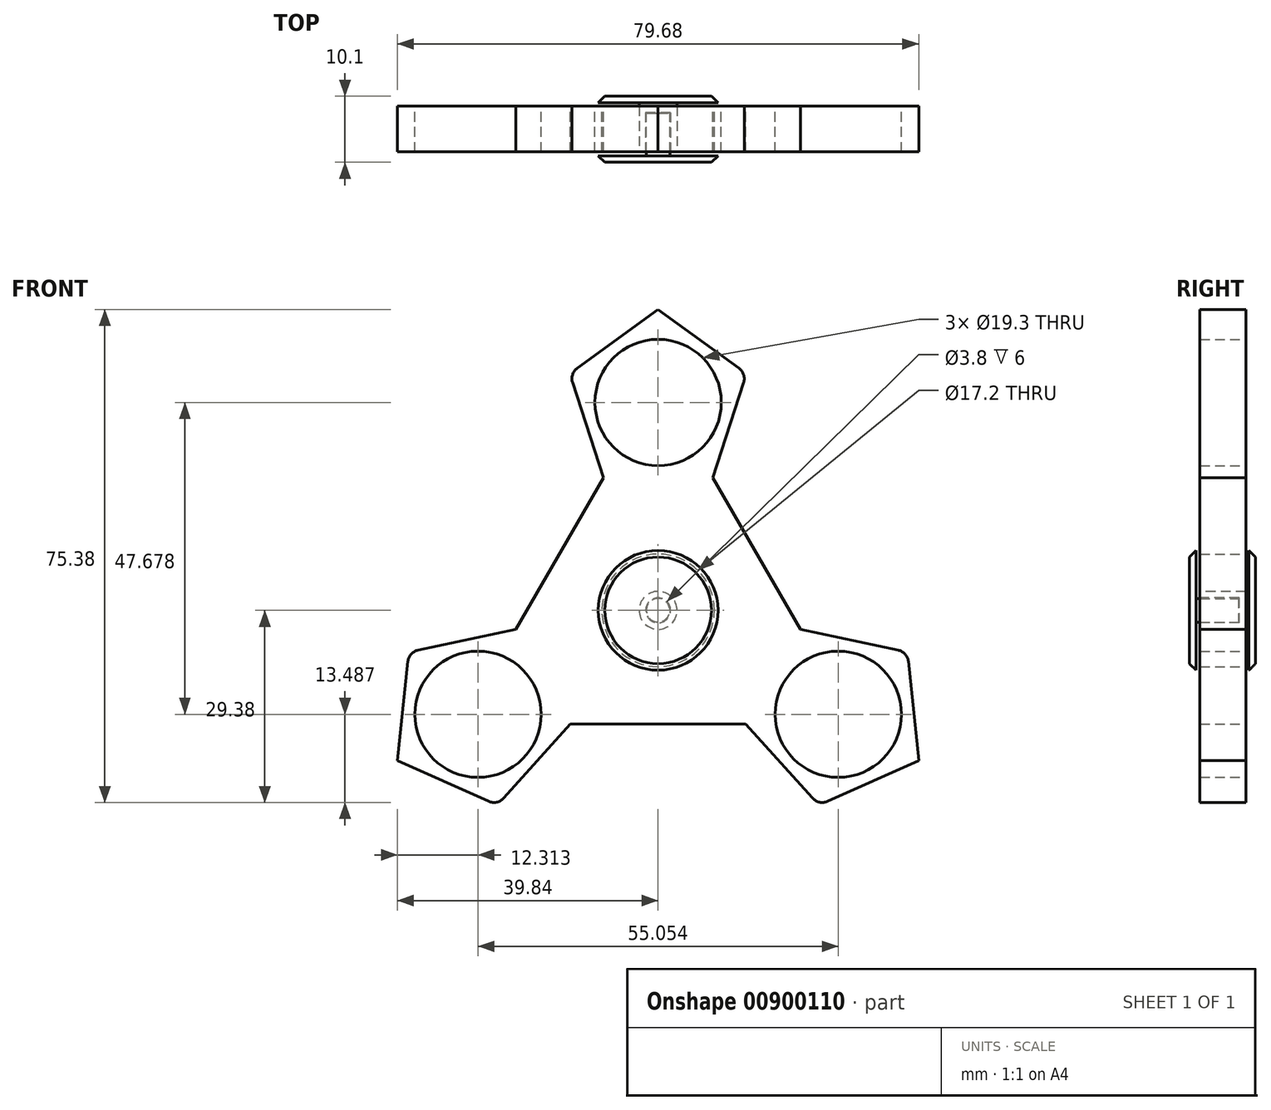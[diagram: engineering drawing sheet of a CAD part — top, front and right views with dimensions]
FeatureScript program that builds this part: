
annotation { "Feature Type Name" : "Feature", "Feature Type Description" : "" }
export const myFeature = defineFeature(function(context is Context, id is Id, definition is map)
    precondition{}
    {
        {
            var Q0;
            Q0=qCreatedBy(makeId("Front.planeOp"),FACE);
            var sketch = newSketch(context, id + "F0", { "sketchPlane" : qUnion([Q0])});
            skLineSegment(sketch, "E0", {"start": v(0, 0) * mm, "end": v(0, 31.79) * mm, "construction": true});
            skCircle(sketch, "E1", {"center": v(0, 0) * mm, "radius": 8.6 * mm});
            skCircle(sketch, "E2.cCircle", {"center": v(0, 31.79) * mm, "radius": 11.5 * mm, "construction": true});
            skLineSegment(sketch, "E2.0", {"start": v(13.52, 36.18) * mm, "end": v(8.36, 20.29) * mm});
            skLineSegment(sketch, "E2.1", {"start": v(8.36, 20.29) * mm, "end": v(-8.36, 20.29) * mm});
            skLineSegment(sketch, "E2.2", {"start": v(-8.36, 20.29) * mm, "end": v(-13.52, 36.18) * mm});
            skLineSegment(sketch, "E2.3", {"start": v(-13.52, 36.18) * mm, "end": v(0, 46) * mm});
            skLineSegment(sketch, "E2.4", {"start": v(0, 46) * mm, "end": v(13.52, 36.18) * mm});
            skPoint(sketch, "E2.0.midPoint", {"position": v(10.94, 28.23) * mm});
            skArc(sketch, "E3", {"start": v(-13.02, 9.3) * mm, "mid": v(0, -16) * mm, "end": v(13.02, 9.3) * mm});
            skLineSegment(sketch, "E4", {"start": v(13.92, 8.04) * mm, "end": v(14.57, 6.62) * mm});
            skLineSegment(sketch, "E5", {"start": v(-13.92, 8.04) * mm, "end": v(-14.57, 6.62) * mm});
            skCircle(sketch, "E6", {"center": v(0, 31.79) * mm, "radius": 9.65 * mm});
            skLineSegment(sketch, "E7.1.0", {"start": v(-39.84, -23) * mm, "end": v(-38.1, -6.38) * mm});
            skLineSegment(sketch, "E7.1.1", {"start": v(-24.57, -29.8) * mm, "end": v(-39.84, -23) * mm});
            skLineSegment(sketch, "E7.1.2", {"start": v(-13.39, -17.38) * mm, "end": v(-24.57, -29.8) * mm});
            skLineSegment(sketch, "E7.1.3", {"start": v(-38.1, -6.38) * mm, "end": v(-21.75, -2.9) * mm});
            skLineSegment(sketch, "E7.1.4", {"start": v(-13.92, 8.04) * mm, "end": v(-13.02, 9.3) * mm});
            skLineSegment(sketch, "E7.1.5", {"start": v(0, -16.08) * mm, "end": v(1.55, -15.92) * mm});
            skArc(sketch, "E7.1.6", {"start": v(-13.02, 9.3) * mm, "mid": v(-13.86, 8) * mm, "end": v(-14.57, 6.62) * mm});
            skCircle(sketch, "E7.1.7", {"center": v(-27.53, -15.9) * mm, "radius": 9.65 * mm});
            skLineSegment(sketch, "E7.2.0", {"start": v(39.84, -23) * mm, "end": v(24.57, -29.8) * mm});
            skLineSegment(sketch, "E7.2.1", {"start": v(38.1, -6.38) * mm, "end": v(39.84, -23) * mm});
            skLineSegment(sketch, "E7.2.2", {"start": v(21.75, -2.9) * mm, "end": v(38.1, -6.38) * mm});
            skLineSegment(sketch, "E7.2.3", {"start": v(24.57, -29.8) * mm, "end": v(13.39, -17.38) * mm});
            skLineSegment(sketch, "E7.2.4", {"start": v(0, -16.08) * mm, "end": v(-1.55, -15.92) * mm});
            skLineSegment(sketch, "E7.2.5", {"start": v(13.92, 8.04) * mm, "end": v(13.02, 9.3) * mm});
            skCircle(sketch, "E7.2.6", {"center": v(0, 0) * mm, "radius": 16 * mm});
            skCircle(sketch, "E7.2.7", {"center": v(27.53, -15.9) * mm, "radius": 9.65 * mm});
            skArc(sketch, "E8.trimOffspring", {"start": v(-1.55, -15.92) * mm, "mid": v(13.86, -8) * mm, "end": v(13.02, 9.3) * mm});
            skLineSegment(sketch, "E9", {"start": v(-8.36, 20.29) * mm, "end": v(-21.75, -2.9) * mm});
            skLineSegment(sketch, "E10", {"start": v(-13.39, -17.38) * mm, "end": v(13.39, -17.38) * mm});
            skLineSegment(sketch, "E11", {"start": v(8.36, 20.29) * mm, "end": v(21.75, -2.9) * mm});
            skPoint(sketch, "E12.orphan", {"position": v(-13.39, -17.38) * mm});
            skPoint(sketch, "E13.orphan", {"position": v(21.75, -2.9) * mm});
            skSolve(sketch);
        }
        {
            var Q0;
            {var subQ0=sQuery(id+"F0.wireOp",EDGE,"E5");Q0=makeQuery(id+"F0.imprint","IMPRINT",FACE,{"disambiguationData":[TD([[makeQuery(id+"F0.imprint","IMPRINT",EDGE,{"derivedFrom":subQ0}),1.0]])]});}
            var Q1;
            {var subQ0=sQuery(id+"F0.wireOp",EDGE,"E4");Q1=makeQuery(id+"F0.imprint","IMPRINT",FACE,{"disambiguationData":[TD([[makeQuery(id+"F0.imprint","IMPRINT",EDGE,{"derivedFrom":subQ0}),-1.0]])]});}
            var Q2;
            {var subQ0=sQuery(id+"F0.wireOp",EDGE,"E7.1.5");Q2=makeQuery(id+"F0.imprint","IMPRINT",FACE,{"disambiguationData":[TD([[makeQuery(id+"F0.imprint","IMPRINT",EDGE,{"derivedFrom":subQ0}),1.0]])]});}
            var Q3;
            Q3=makeQuery(id+"F0.imprint","IMPRINT",FACE,{"disambiguationData":[TD([[makeQuery(id+"F0.imprint","IMPRINT",EDGE,{"derivedFrom":sQuery(id+"F0.wireOp",EDGE,"E2.1")}),1.0]])]});
            var Q4;
            Q4=makeQuery(id+"F0.imprint","IMPRINT",FACE,{"disambiguationData":[TD([[makeQuery(id+"F0.imprint","IMPRINT",EDGE,{"derivedFrom":sQuery(id+"F0.wireOp",EDGE,"E1")}),-1.0]])]});
            var Q5;
            Q5=makeQuery(id+"F0.imprint","IMPRINT",FACE,{"disambiguationData":[TD([[makeQuery(id+"F0.imprint","IMPRINT",EDGE,{"derivedFrom":sQuery(id+"F0.wireOp",EDGE,"E2.0")}),-1.0]])]});
            extrude(context, id + "F1", {"entities" : qUnion([Q0, Q1, Q2, Q3, Q4, Q5]), "depth" : 7 * mm, "offsetDistance" : 25 * mm});
        }
        {
            var Q0;
            Q0=makeQuery(id+"F1.opExtrude","SWEPT_EDGE",EDGE,{"disambiguationData":[OSD([sQuery(id+"F0.wireOp",EDGE,"E2.2"),sQuery(id+"F0.wireOp",EDGE,"E2.3")])]});
            fillet(context, id + "F2", {"entities" : qUnion([Q0]), "radius" : 2 * mm, "tangentPropagation" : true, "allowEdgeOverflow" : false});
        }
        {
            var Q0;
            Q0=makeQuery(id+"F1.opExtrude","SWEPT_EDGE",EDGE,{"disambiguationData":[OSD([sQuery(id+"F0.wireOp",EDGE,"E2.0"),sQuery(id+"F0.wireOp",EDGE,"E2.4")])]});
            var Q1;
            Q1=makeQuery(id+"F1.opExtrude","SWEPT_EDGE",EDGE,{"disambiguationData":[OSD([sQuery(id+"F0.wireOp",EDGE,"E7.2.1"),sQuery(id+"F0.wireOp",EDGE,"E7.2.2")])]});
            var Q2;
            Q2=makeQuery(id+"F1.opExtrude","SWEPT_EDGE",EDGE,{"disambiguationData":[OSD([sQuery(id+"F0.wireOp",EDGE,"E7.2.0"),sQuery(id+"F0.wireOp",EDGE,"E7.2.3")])]});
            var Q3;
            Q3=makeQuery(id+"F1.opExtrude","SWEPT_EDGE",EDGE,{"disambiguationData":[OSD([sQuery(id+"F0.wireOp",EDGE,"E7.1.0"),sQuery(id+"F0.wireOp",EDGE,"E7.1.3")])]});
            var Q4;
            Q4=makeQuery(id+"F1.opExtrude","SWEPT_EDGE",EDGE,{"disambiguationData":[OSD([sQuery(id+"F0.wireOp",EDGE,"E7.1.1"),sQuery(id+"F0.wireOp",EDGE,"E7.1.2")])]});
            fillet(context, id + "F3", {"entities" : qUnion([Q0, Q1, Q2, Q3, Q4]), "radius" : 2 * mm, "tangentPropagation" : true, "allowEdgeOverflow" : false});
        }
        {
            var Q0;
            Q0=qCreatedBy(makeId("Top.planeOp"),FACE);
            var sketch = newSketch(context, id + "F4", { "sketchPlane" : qUnion([Q0])});
            skPoint(sketch, "E14.0", {"position": v(0, 0) * mm});
            skLineSegment(sketch, "E15", {"start": v(0, 0) * mm, "end": v(-2.9, 0) * mm, "construction": true});
            skLineSegment(sketch, "E16", {"start": v(-2.9, 0) * mm, "end": v(-2.9, -7) * mm});
            skLineSegment(sketch, "E17", {"start": v(-9.15, 1.5) * mm, "end": v(-9.15, 0.5) * mm});
            skLineSegment(sketch, "E18", {"start": v(-9.15, 0.5) * mm, "end": v(-2.9, 0.5) * mm});
            skLineSegment(sketch, "E19", {"start": v(-2.9, 0.5) * mm, "end": v(-2.9, 0) * mm});
            skLineSegment(sketch, "E20", {"start": v(-2.9, -7) * mm, "end": v(-1.9, -7) * mm});
            skLineSegment(sketch, "E21", {"start": v(-1.9, -7) * mm, "end": v(-1.9, -1) * mm});
            skLineSegment(sketch, "E22", {"start": v(-1.9, -1) * mm, "end": v(0, -1) * mm});
            skLineSegment(sketch, "E23", {"start": v(0, -1) * mm, "end": v(0, 1.5) * mm});
            skLineSegment(sketch, "E24", {"start": v(0, 1.5) * mm, "end": v(-9.15, 1.5) * mm});
            skSolve(sketch);
        }
        {
            var Q0;
            Q0=makeQuery(id+"F4.imprint","IMPRINT",FACE,{"disambiguationData":[TD([[makeQuery(id+"F4.imprint","IMPRINT",EDGE,{"derivedFrom":sQuery(id+"F4.wireOp",EDGE,"E16")}),1.0]])]});
            var Q1;
            Q1=sQuery(id+"F4.wireOp",EDGE,"E23");
            revolve(context, id + "F5", {"surfaceOperationType" : NewSurfaceOperationType.NEW, "entities" : qUnion([Q0]), "axis" : qUnion([Q1]), "revolveType" : RevolveType.FULL});
        }
        {
            var Q0;
            Q0=makeQuery(id+"F5.opRevolve","SWEPT_EDGE",EDGE,{"disambiguationData":[OSD([sQuery(id+"F4.wireOp",EDGE,"E17"),sQuery(id+"F4.wireOp",EDGE,"E24")])]});
            chamfer(context, id + "F6", {"entities" : qUnion([Q0]), "width" : 1 * mm, "tangentPropagation" : true});
        }
        {
            var Q0;
            Q0=qCreatedBy(makeId("Top.planeOp"),FACE);
            var sketch = newSketch(context, id + "F7", { "sketchPlane" : qUnion([Q0])});
            skLineSegment(sketch, "E25", {"start": v(0, 0) * mm, "end": v(0, -9.33) * mm, "construction": true});
            skLineSegment(sketch, "E26.0", {"start": v(1.9, -7) * mm, "end": v(-1.9, -7) * mm});
            skLineSegment(sketch, "E27", {"start": v(0, -7) * mm, "end": v(-1.9, -7) * mm});
            skLineSegment(sketch, "E28", {"start": v(-1.9, -7) * mm, "end": v(-1.8, -7) * mm, "construction": true});
            skLineSegment(sketch, "E29", {"start": v(-1.8, -7) * mm, "end": v(-1.8, -1.1) * mm});
            skLineSegment(sketch, "E30", {"start": v(-1.8, -1.1) * mm, "end": v(0, -1.1) * mm});
            skLineSegment(sketch, "E31", {"start": v(0, -1.1) * mm, "end": v(0, -8.6) * mm});
            skLineSegment(sketch, "E32", {"start": v(0, -8.6) * mm, "end": v(-9.15, -8.6) * mm});
            skLineSegment(sketch, "E33", {"start": v(-9.15, -8.6) * mm, "end": v(-9.15, -7.6) * mm});
            skLineSegment(sketch, "E34", {"start": v(-9.15, -7.6) * mm, "end": v(-1.8, -7.6) * mm});
            skLineSegment(sketch, "E35", {"start": v(-1.8, -7.6) * mm, "end": v(-1.8, -7) * mm});
            skSolve(sketch);
        }
        {
            var Q0;
            {var subQ3=sQuery(id+"F7.wireOp",EDGE,"E32");Q0=makeQuery(id+"F7.imprint","IMPRINT",FACE,{"disambiguationData":[TD([[makeQuery(id+"F7.imprint","IMPRINT",EDGE,{"derivedFrom":subQ3}),-1.0]])]});}
            var Q1;
            {var subQ3=sQuery(id+"F7.wireOp",EDGE,"E29");Q1=makeQuery(id+"F7.imprint","IMPRINT",FACE,{"disambiguationData":[TD([[makeQuery(id+"F7.imprint","IMPRINT",EDGE,{"derivedFrom":subQ3}),-1.0]])]});}
            var Q2;
            Q2=sQuery(id+"F7.wireOp",EDGE,"E31");
            revolve(context, id + "F8", {"operationType" : NewBodyOperationType.ADD, "surfaceOperationType" : NewSurfaceOperationType.NEW, "entities" : qUnion([Q0, Q1]), "axis" : qUnion([Q2]), "revolveType" : RevolveType.FULL});
        }
        {
            var Q0;
            Q0=makeQuery(id+"F8.opRevolve","SWEPT_EDGE",EDGE,{"disambiguationData":[OSD([sQuery(id+"F7.wireOp",EDGE,"E32"),sQuery(id+"F7.wireOp",EDGE,"E33")])]});
            chamfer(context, id + "F9", {"entities" : qUnion([Q0]), "width" : 1 * mm, "tangentPropagation" : true});
        }
    });
